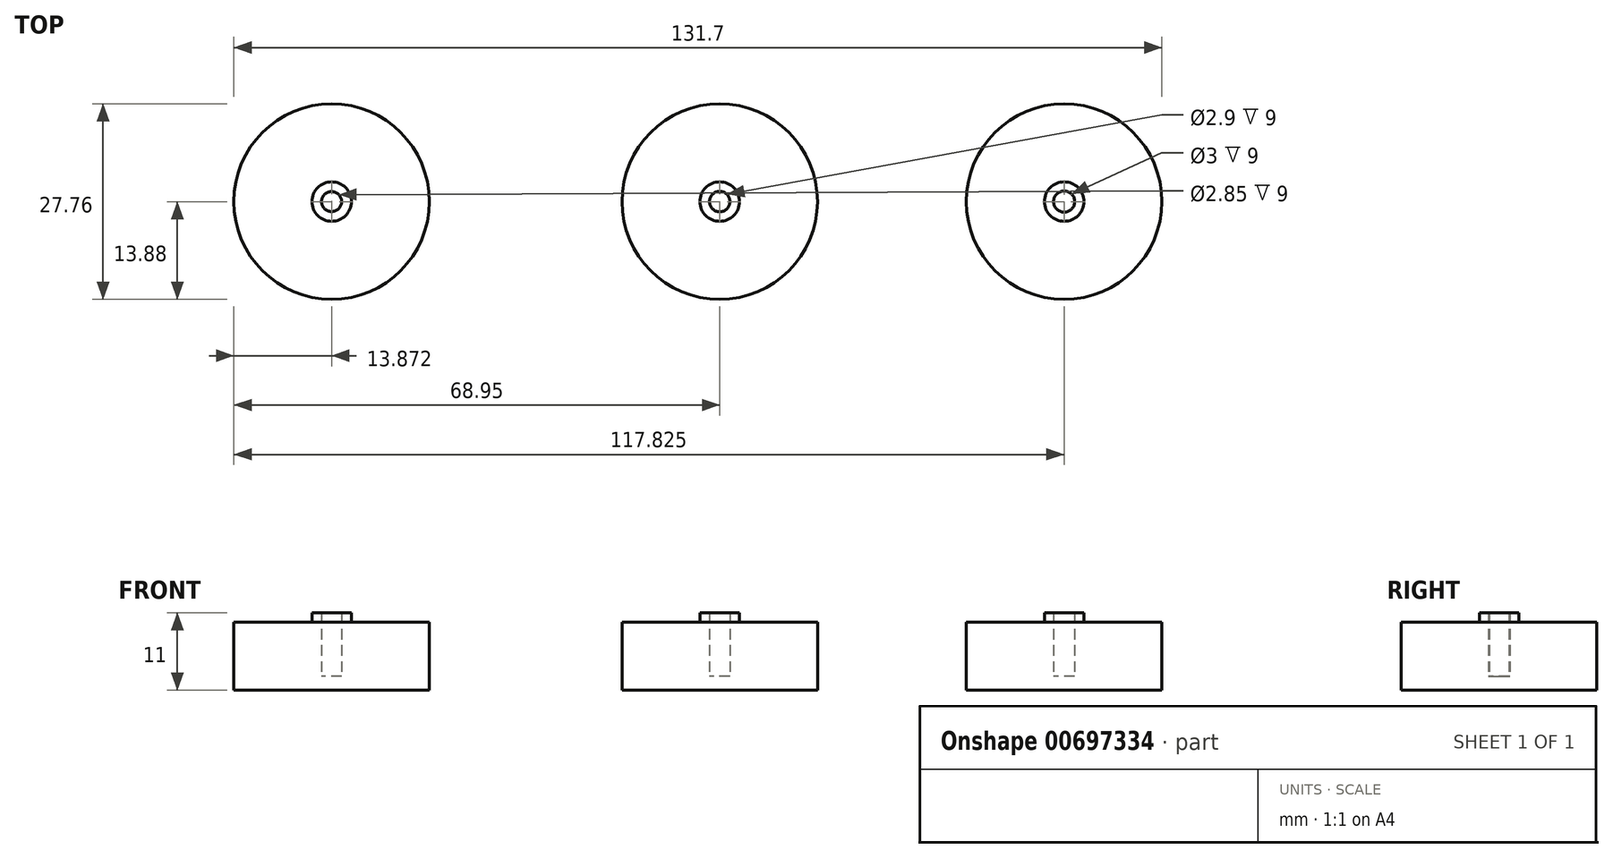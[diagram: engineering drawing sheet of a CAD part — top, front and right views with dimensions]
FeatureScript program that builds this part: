
annotation { "Feature Type Name" : "Feature", "Feature Type Description" : "" }
export const myFeature = defineFeature(function(context is Context, id is Id, definition is map)
    precondition{}
    {
        {
            var Q0;
            Q0=qCreatedBy(makeId("Top.planeOp"),FACE);
            var sketch = newSketch(context, id + "F0", { "sketchPlane" : qUnion([Q0])});
            skCircle(sketch, "E0", {"center": v(0, 0) * mm, "radius": 13.88 * mm});
            skCircle(sketch, "E1", {"center": v(0, 0) * mm, "radius": 2.8 * mm});
            skCircle(sketch, "E2", {"center": v(0, 0) * mm, "radius": 1.45 * mm});
            skCircle(sketch, "E3", {"center": v(48.88, 0) * mm, "radius": 13.88 * mm});
            skCircle(sketch, "E4", {"center": v(48.88, 0) * mm, "radius": 2.8 * mm});
            skCircle(sketch, "E5", {"center": v(48.88, 0) * mm, "radius": 1.5 * mm});
            skCircle(sketch, "E6", {"center": v(-55.08, 0) * mm, "radius": 13.88 * mm});
            skCircle(sketch, "E7", {"center": v(-55.08, 0) * mm, "radius": 2.8 * mm});
            skCircle(sketch, "E8", {"center": v(-55.08, 0) * mm, "radius": 1.43 * mm});
            skSolve(sketch);
        }
        {
            var Q0;
            Q0 = qSketchRegion(id + "F0", true);
            var Q1;
            Q1=makeQuery(id+"F0.imprint","IMPRINT",FACE,{"disambiguationData":[TD([[makeQuery(id+"F0.imprint","IMPRINT",EDGE,{"derivedFrom":sQuery(id+"F0.wireOp",EDGE,"E1")}),1.0]])]});
            var Q2;
            Q2=makeQuery(id+"F0.imprint","IMPRINT",FACE,{"disambiguationData":[TD([[makeQuery(id+"F0.imprint","IMPRINT",EDGE,{"derivedFrom":sQuery(id+"F0.wireOp",EDGE,"E2")}),1.0]])]});
            var Q3;
            Q3=makeQuery(id+"F0.imprint","IMPRINT",FACE,{"disambiguationData":[TD([[makeQuery(id+"F0.imprint","IMPRINT",EDGE,{"derivedFrom":sQuery(id+"F0.wireOp",EDGE,"E7")}),1.0]])]});
            var Q4;
            Q4=makeQuery(id+"F0.imprint","IMPRINT",FACE,{"disambiguationData":[TD([[makeQuery(id+"F0.imprint","IMPRINT",EDGE,{"derivedFrom":sQuery(id+"F0.wireOp",EDGE,"E8")}),1.0]])]});
            var Q5;
            Q5=makeQuery(id+"F0.imprint","IMPRINT",FACE,{"disambiguationData":[TD([[makeQuery(id+"F0.imprint","IMPRINT",EDGE,{"derivedFrom":sQuery(id+"F0.wireOp",EDGE,"E4")}),1.0]])]});
            var Q6;
            Q6=makeQuery(id+"F0.imprint","IMPRINT",FACE,{"disambiguationData":[TD([[makeQuery(id+"F0.imprint","IMPRINT",EDGE,{"derivedFrom":sQuery(id+"F0.wireOp",EDGE,"E5")}),1.0]])]});
            extrude(context, id + "F1", {"entities" : qUnion([Q0, Q1, Q2, Q3, Q4, Q5, Q6]), "oppositeDirection" : true, "depth" : 9.65 * mm, "offsetDistance" : 25 * mm});
        }
        {
            var Q0;
            Q0=makeQuery(id+"F0.imprint","IMPRINT",FACE,{"disambiguationData":[TD([[makeQuery(id+"F0.imprint","IMPRINT",EDGE,{"derivedFrom":sQuery(id+"F0.wireOp",EDGE,"E1")}),1.0]])]});
            var Q1;
            Q1=makeQuery(id+"F0.imprint","IMPRINT",FACE,{"disambiguationData":[TD([[makeQuery(id+"F0.imprint","IMPRINT",EDGE,{"derivedFrom":sQuery(id+"F0.wireOp",EDGE,"E4")}),1.0]])]});
            var Q2;
            Q2=makeQuery(id+"F0.imprint","IMPRINT",FACE,{"disambiguationData":[TD([[makeQuery(id+"F0.imprint","IMPRINT",EDGE,{"derivedFrom":sQuery(id+"F0.wireOp",EDGE,"E7")}),1.0]])]});
            extrude(context, id + "F2", {"entities" : qUnion([Q0, Q1, Q2]), "operationType" : NewBodyOperationType.ADD, "depth" : (11 - 9.65) * mm, "offsetDistance" : 25 * mm});
        }
        {
            var Q0;
            Q0=makeQuery(id+"F0.imprint","IMPRINT",FACE,{"disambiguationData":[TD([[makeQuery(id+"F0.imprint","IMPRINT",EDGE,{"derivedFrom":sQuery(id+"F0.wireOp",EDGE,"E2")}),1.0]])]});
            var Q1;
            Q1=makeQuery(id+"F0.imprint","IMPRINT",FACE,{"disambiguationData":[TD([[makeQuery(id+"F0.imprint","IMPRINT",EDGE,{"derivedFrom":sQuery(id+"F0.wireOp",EDGE,"E8")}),1.0]])]});
            var Q2;
            Q2=makeQuery(id+"F0.imprint","IMPRINT",FACE,{"disambiguationData":[TD([[makeQuery(id+"F0.imprint","IMPRINT",EDGE,{"derivedFrom":sQuery(id+"F0.wireOp",EDGE,"E5")}),1.0]])]});
            extrude(context, id + "F3", {"entities" : qUnion([Q0, Q1, Q2]), "operationType" : NewBodyOperationType.REMOVE, "oppositeDirection" : true, "depth" : 7.65 * mm, "offsetDistance" : 25 * mm});
        }
    });
